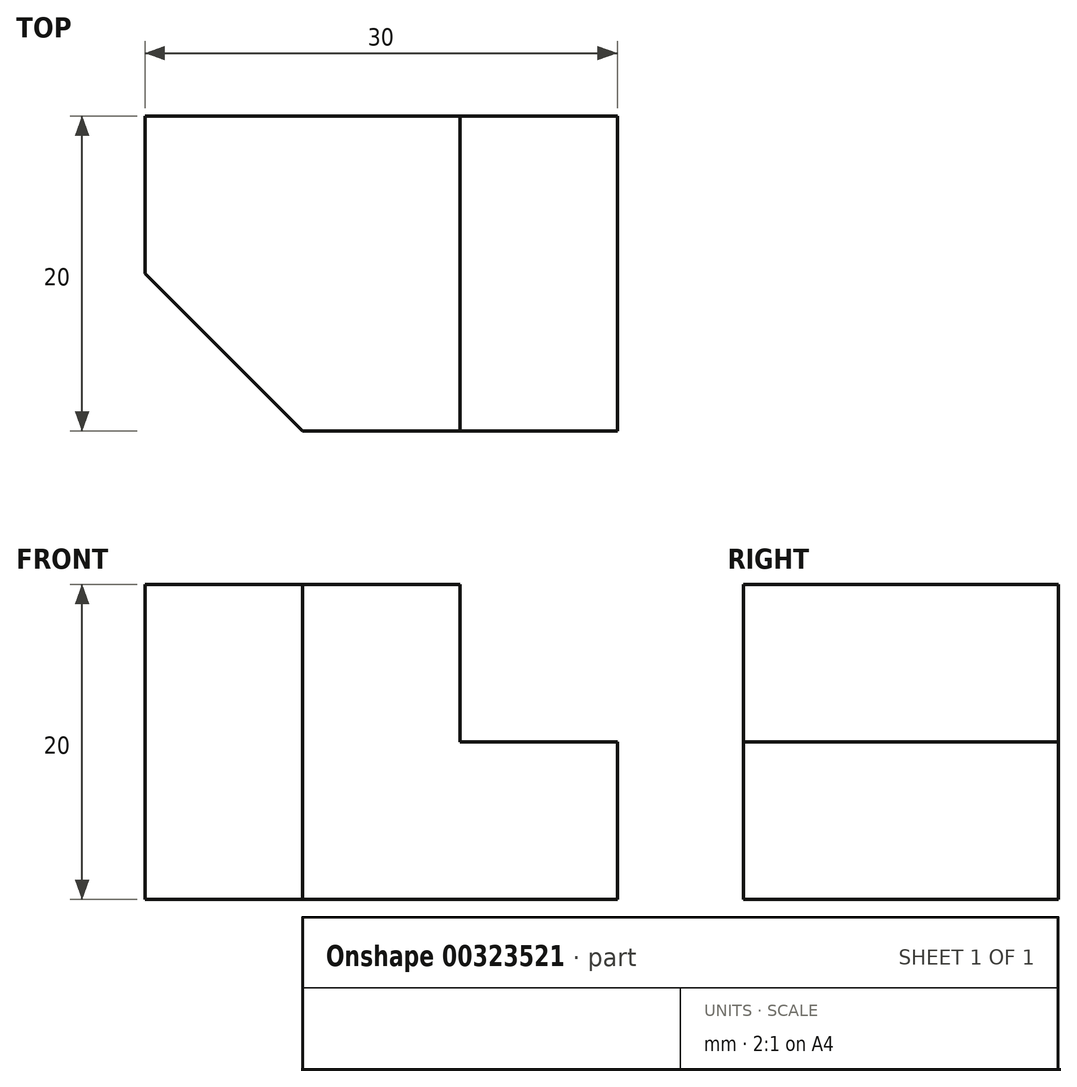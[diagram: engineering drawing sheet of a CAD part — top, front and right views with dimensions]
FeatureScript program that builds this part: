
annotation { "Feature Type Name" : "Feature", "Feature Type Description" : "" }
export const myFeature = defineFeature(function(context is Context, id is Id, definition is map)
    precondition{}
    {
        {
            var Q0;
            Q0=qCreatedBy(makeId("Front.planeOp"),FACE);
            var sketch = newSketch(context, id + "F0", { "sketchPlane" : qUnion([Q0])});
            skLineSegment(sketch, "E0", {"start": v(0, 0) * mm, "end": v(30, 0) * mm});
            skLineSegment(sketch, "E1", {"start": v(30, 0) * mm, "end": v(30, 20) * mm});
            skLineSegment(sketch, "E2", {"start": v(30, 20) * mm, "end": v(0, 20) * mm});
            skLineSegment(sketch, "E3", {"start": v(0, 20) * mm, "end": v(0, 0) * mm});
            skSolve(sketch);
        }
        {
            var Q0;
            Q0=makeQuery(id+"F0.imprint","IMPRINT",FACE,{"disambiguationData":[TD([[makeQuery(id+"F0.imprint","IMPRINT",EDGE,{"derivedFrom":sQuery(id+"F0.wireOp",EDGE,"E0")}),1.0]])]});
            extrude(context, id + "F1", {"entities" : qUnion([Q0]), "oppositeDirection" : true, "depth" : 20 * mm});
        }
        {
            var Q0;
            Q0=makeQuery(id+"F1.opExtrude","SWEPT_FACE",FACE,{"disambiguationData":[OSD([sQuery(id+"F0.wireOp",EDGE,"E2")])]});
            var sketch = newSketch(context, id + "F2", { "sketchPlane" : qUnion([Q0])});
            skLineSegment(sketch, "E4", {"start": v(0, 0) * mm, "end": v(10, 0) * mm});
            skLineSegment(sketch, "E5", {"start": v(10, 0) * mm, "end": v(0, 10) * mm});
            skLineSegment(sketch, "E6", {"start": v(0, 10) * mm, "end": v(0, 0) * mm});
            skSolve(sketch);
        }
        {
            var Q0;
            Q0=makeQuery(id+"F2.imprint","IMPRINT",FACE,{"disambiguationData":[TD([[makeQuery(id+"F2.imprint","IMPRINT",EDGE,{"derivedFrom":sQuery(id+"F2.wireOp",EDGE,"E4")}),-1.0]])]});
            extrude(context, id + "F3", {"entities" : qUnion([Q0]), "operationType" : NewBodyOperationType.REMOVE, "oppositeDirection" : true, "depth" : 25 * mm});
        }
        {
            var Q0;
            Q0=makeQuery(id+"F1.opExtrude","SWEPT_FACE",FACE,{"disambiguationData":[OSD([sQuery(id+"F0.wireOp",EDGE,"E2")])]});
            var sketch = newSketch(context, id + "F4", { "sketchPlane" : qUnion([Q0])});
            skLineSegment(sketch, "E7", {"start": v(30, 0) * mm, "end": v(20, 0) * mm});
            skLineSegment(sketch, "E8", {"start": v(20, 0) * mm, "end": v(20, 20) * mm});
            skLineSegment(sketch, "E9", {"start": v(20, 20) * mm, "end": v(30, 20) * mm});
            skLineSegment(sketch, "E10", {"start": v(30, 20) * mm, "end": v(30, 0) * mm});
            skSolve(sketch);
        }
        {
            var Q0;
            Q0=makeQuery(id+"F4.imprint","IMPRINT",FACE,{"disambiguationData":[TD([[makeQuery(id+"F4.imprint","IMPRINT",EDGE,{"derivedFrom":sQuery(id+"F4.wireOp",EDGE,"E7")}),-1.0]])]});
            extrude(context, id + "F5", {"entities" : qUnion([Q0]), "operationType" : NewBodyOperationType.REMOVE, "oppositeDirection" : true, "depth" : 10 * mm});
        }
    });
